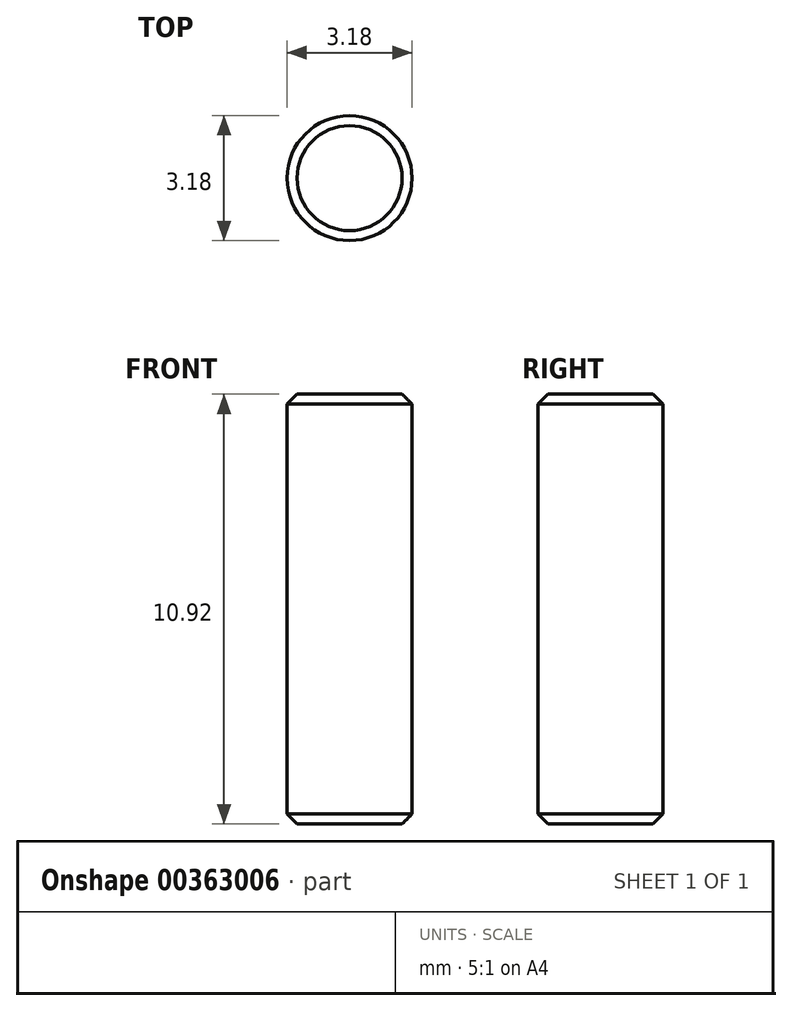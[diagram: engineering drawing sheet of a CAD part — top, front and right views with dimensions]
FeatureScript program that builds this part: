
annotation { "Feature Type Name" : "Feature", "Feature Type Description" : "" }
export const myFeature = defineFeature(function(context is Context, id is Id, definition is map)
    precondition{}
    {
        {
            var Q0;
            Q0=qCreatedBy(makeId("Top.planeOp"),FACE);
            var sketch = newSketch(context, id + "F0", { "sketchPlane" : qUnion([Q0])});
            skCircle(sketch, "E0", {"center": v(0, 0) * mm, "radius": 1.59 * mm});
            skSolve(sketch);
        }
        {
            var Q0;
            Q0=makeQuery(id+"F0.imprint","IMPRINT",FACE,{"disambiguationData":[TD([[makeQuery(id+"F0.imprint","IMPRINT",EDGE,{"derivedFrom":sQuery(id+"F0.wireOp",EDGE,"E0")}),1.0]])]});
            extrude(context, id + "F1", {"entities" : qUnion([Q0]), "depth" : 10.92 * mm});
        }
        {
            var Q0;
            Q0=makeQuery(id+"F1.opExtrude","CAP_EDGE",EDGE,{"disambiguationData":[OSD([sQuery(id+"F0.wireOp",EDGE,"E0")])],"isStart":false});
            var Q1;
            Q1=makeQuery(id+"F1.opExtrude","CAP_EDGE",EDGE,{"disambiguationData":[OSD([sQuery(id+"F0.wireOp",EDGE,"E0")])],"isStart":true});
            chamfer(context, id + "F2", {"entities" : qUnion([Q0, Q1]), "chamferType" : ChamferType.OFFSET_ANGLE, "width" : 0.25 * mm, "oppositeDirection" : false, "angle" : 45 * degree, "tangentPropagation" : true});
        }
    });
